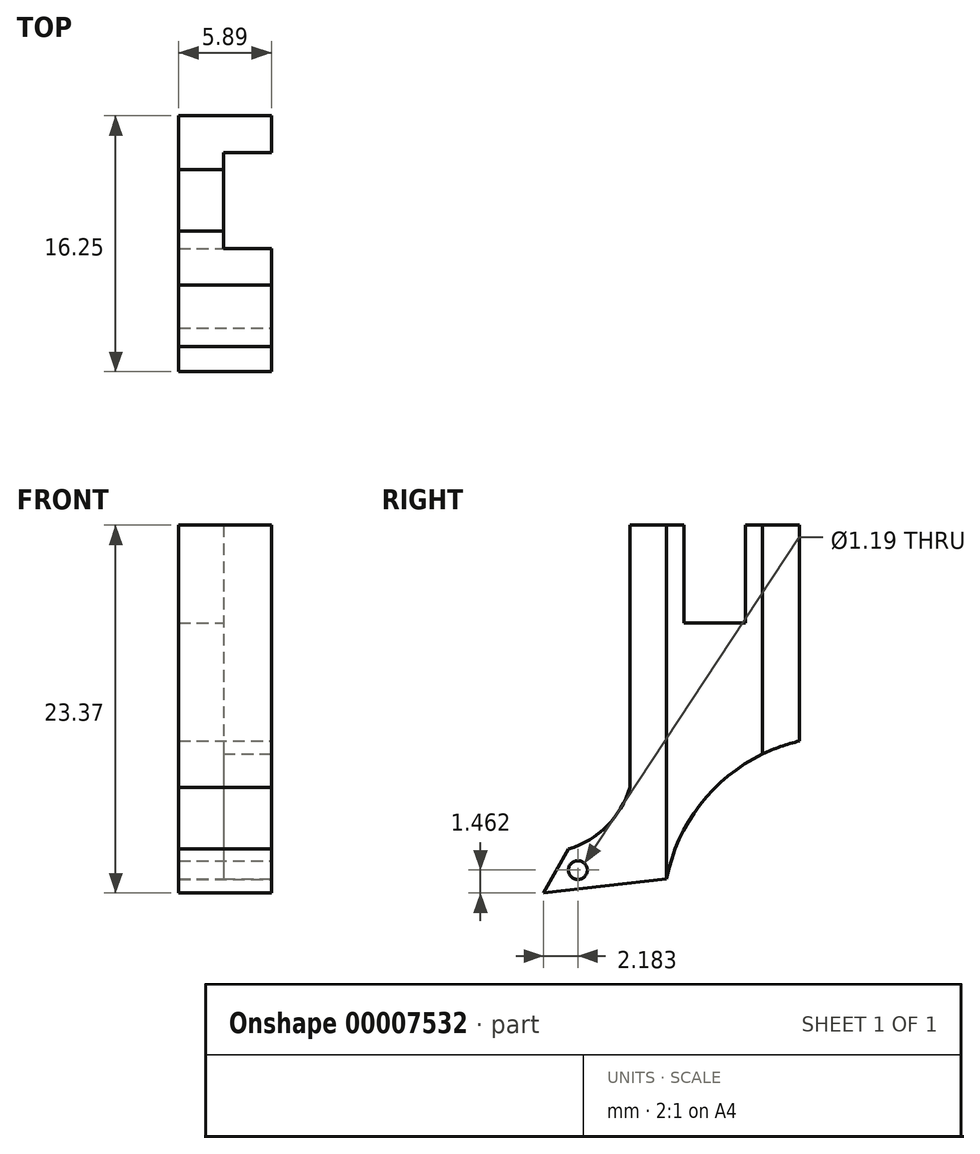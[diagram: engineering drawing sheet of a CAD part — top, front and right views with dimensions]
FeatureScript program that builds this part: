
annotation { "Feature Type Name" : "Feature", "Feature Type Description" : "" }
export const myFeature = defineFeature(function(context is Context, id is Id, definition is map)
    precondition{}
    {
        {
            var Q0;
            Q0=qCreatedBy(makeId("Right.planeOp"),FACE);
            var sketch = newSketch(context, id + "F0", { "sketchPlane" : qUnion([Q0])});
            skLineSegment(sketch, "E0", {"start": v(0, 32.46) * mm, "end": v(0, -41.99) * mm, "construction": true});
            skLineSegment(sketch, "E1", {"start": v(5.38, 20.85) * mm, "end": v(5.38, -12.47) * mm});
            skLineSegment(sketch, "E2.0.MirrorCS", {"start": v(-5.38, 20.85) * mm, "end": v(-5.38, -12.47) * mm});
            skLineSegment(sketch, "E3", {"start": v(-21.69, -19.18) * mm, "end": v(18.7, -19.18) * mm, "construction": true});
            skLineSegment(sketch, "E4", {"start": v(-5.38, 4.2) * mm, "end": v(-1.96, 4.2) * mm});
            skLineSegment(sketch, "E5", {"start": v(-1.96, 4.2) * mm, "end": v(-1.96, -2.03) * mm});
            skLineSegment(sketch, "E6.0.MirrorCS", {"start": v(1.96, 4.2) * mm, "end": v(1.96, -2.03) * mm});
            skLineSegment(sketch, "E7", {"start": v(-1.96, -2.03) * mm, "end": v(1.96, -2.03) * mm});
            skLineSegment(sketch, "E8.trimOffspring", {"start": v(1.96, 4.2) * mm, "end": v(5.38, 4.2) * mm});
            skLineSegment(sketch, "E9", {"start": v(-3.05, 6.58) * mm, "end": v(-3.05, -18.26) * mm});
            skLineSegment(sketch, "E10", {"start": v(-9.6, -9.53) * mm, "end": v(5.38, -9.53) * mm, "construction": true});
            skLineSegment(sketch, "E11", {"start": v(-10.87, -12.93) * mm, "end": v(-10.87, -29.83) * mm, "construction": true});
            skArc(sketch, "E12", {"start": v(5.38, -9.52) * mm, "mid": v(-0.13, -12.65) * mm, "end": v(-3.05, -18.26) * mm});
            skLineSegment(sketch, "E13", {"start": v(-3.05, -18.26) * mm, "end": v(-10.87, -19.18) * mm});
            skLineSegment(sketch, "E14", {"start": v(-8.24, -12.47) * mm, "end": v(8.57, -12.47) * mm, "construction": true});
            skLineSegment(sketch, "E15", {"start": v(-10.87, -19.18) * mm, "end": v(-9.28, -16.38) * mm});
            skLineSegment(sketch, "E16", {"start": v(-19.81, -16.38) * mm, "end": v(20.14, -16.38) * mm, "construction": true});
            skPoint(sketch, "E17", {"position": v(-9.28, -16.38) * mm});
            skArc(sketch, "E18", {"start": v(-9.28, -16.38) * mm, "mid": v(-6.84, -14.92) * mm, "end": v(-5.38, -12.47) * mm});
            skCircle(sketch, "E19", {"center": v(-8.69, -17.72) * mm, "radius": 0.6 * mm});
            skLineSegment(sketch, "E20.0.MirrorCS", {"start": v(3.05, 6.58) * mm, "end": v(3.05, -18.26) * mm});
            skLineSegment(sketch, "E21", {"start": v(-3.05, -18.26) * mm, "end": v(3.05, -18.26) * mm});
            skLineSegment(sketch, "E22", {"start": v(-3.05, 6.58) * mm, "end": v(3.05, 6.58) * mm});
            skSolve(sketch);
        }
        {
            var Q0;
            {var subQ2=sQuery(id+"F0.wireOp",EDGE,"E4");Q0=makeQuery(id+"F0.imprint","IMPRINT",FACE,{"disambiguationData":[TD([[makeQuery(id+"F0.imprint","IMPRINT",EDGE,{"derivedFrom":subQ2}),-1.0]])]});}
            var Q1;
            {var subQ10=sQuery(id+"F0.wireOp",EDGE,"E5");Q1=makeQuery(id+"F0.imprint","IMPRINT",FACE,{"disambiguationData":[TD([[makeQuery(id+"F0.imprint","IMPRINT",EDGE,{"derivedFrom":subQ10}),-1.0]])]});}
            var Q2;
            {var subQ3=sQuery(id+"F0.wireOp",EDGE,"E8.trimOffspring");var subQ5=sQuery(id+"F0.wireOp",EDGE,"E1");var subQ7=makeQuery(id+"F0.imprint","INTERSECT",VERTEX,{"derivedFrom":[subQ5,subQ3]});Q2=makeQuery(id+"F0.imprint","IMPRINT",FACE,{"disambiguationData":[TD([[makeQuery(id+"F0.imprint","IMPRINT",EDGE,{"disambiguationData":[TD([[subQ7,-1.0]])],"derivedFrom":subQ5}),-1.0]])]});}
            extrude(context, id + "F1", {"entities" : qUnion([Q0, Q1, Q2]), "oppositeDirection" : true, "depth" : 5.9 * mm});
        }
        {
            var Q0;
            {var subQ10=sQuery(id+"F0.wireOp",EDGE,"E5");Q0=makeQuery(id+"F0.imprint","IMPRINT",FACE,{"disambiguationData":[TD([[makeQuery(id+"F0.imprint","IMPRINT",EDGE,{"derivedFrom":subQ10}),-1.0]])]});}
            extrude(context, id + "F2", {"entities" : qUnion([Q0]), "operationType" : NewBodyOperationType.REMOVE, "oppositeDirection" : true, "depth" : 3.05 * mm});
        }
    });
